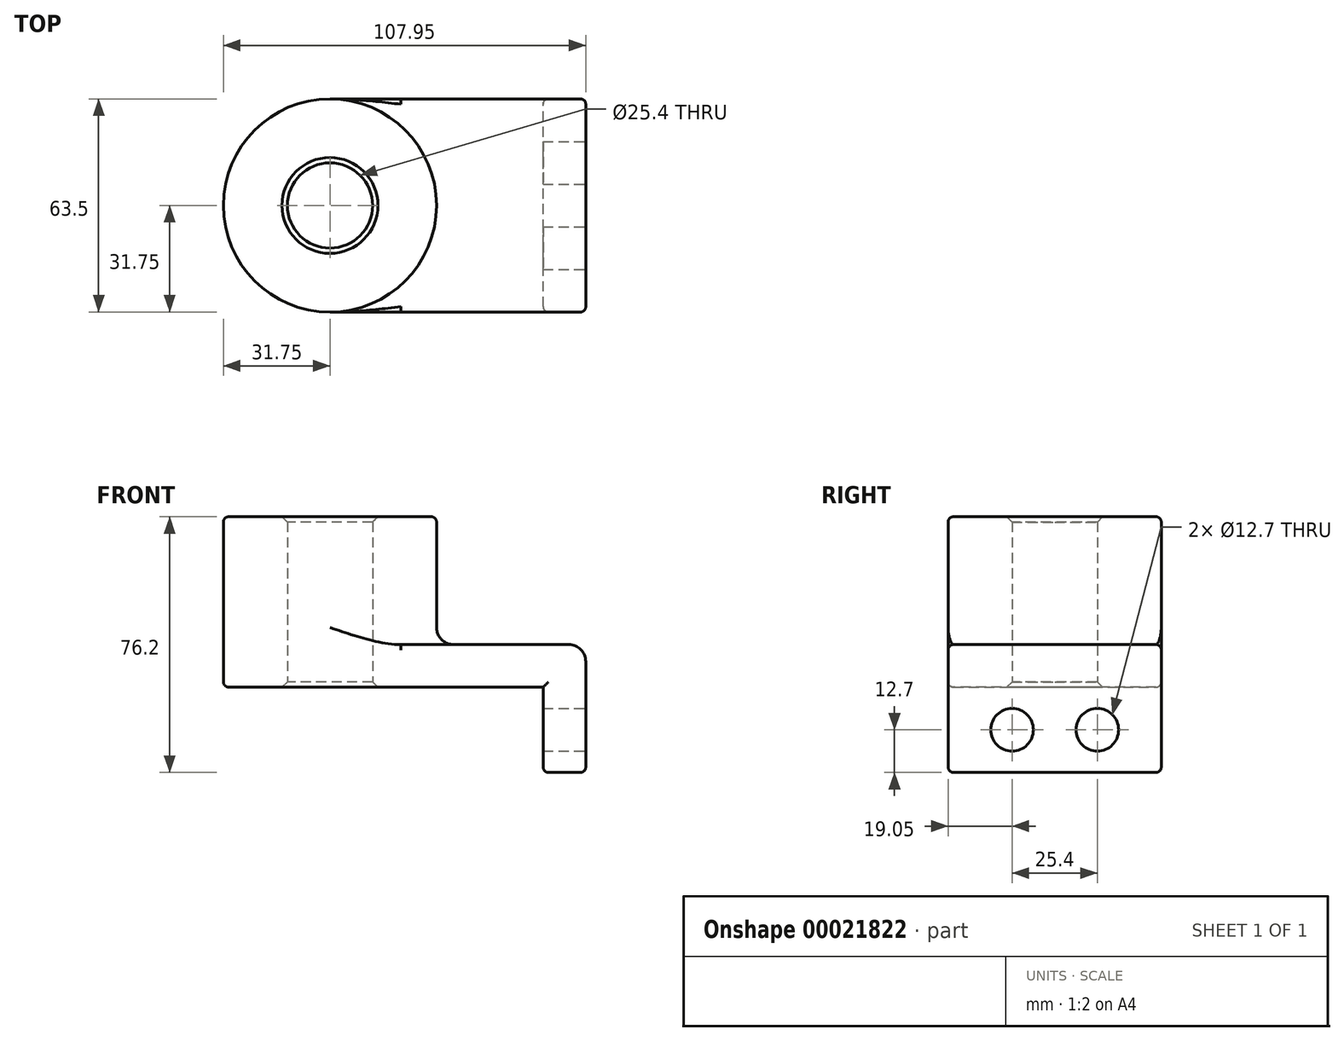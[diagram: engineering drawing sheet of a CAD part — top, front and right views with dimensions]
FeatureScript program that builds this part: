
annotation { "Feature Type Name" : "Feature", "Feature Type Description" : "" }
export const myFeature = defineFeature(function(context is Context, id is Id, definition is map)
    precondition{}
    {
        {
            var Q0;
            Q0=qCreatedBy(makeId("Top.planeOp"),FACE);
            var sketch = newSketch(context, id + "F0", { "sketchPlane" : qUnion([Q0])});
            skLineSegment(sketch, "E0.rect.bottom", {"start": v(38.1, 31.75) * mm, "end": v(-38.1, 31.75) * mm});
            skLineSegment(sketch, "E0.rect.top", {"start": v(38.1, -31.75) * mm, "end": v(-38.1, -31.75) * mm});
            skLineSegment(sketch, "E0.rect.left", {"start": v(38.1, 31.75) * mm, "end": v(38.1, -31.75) * mm});
            skLineSegment(sketch, "E0.rect.right", {"start": v(-38.1, 31.75) * mm, "end": v(-38.1, -31.75) * mm});
            skPoint(sketch, "E0.rect.middle", {"position": v(0, 0) * mm});
            skCircle(sketch, "E1", {"center": v(-38.1, 0) * mm, "radius": 31.75 * mm});
            skCircle(sketch, "E2", {"center": v(-38.1, 0) * mm, "radius": 12.7 * mm});
            skSolve(sketch);
        }
        {
            var Q0;
            Q0 = qSketchRegion(id + "F0", true);
            extrude(context, id + "F1", {"entities" : qUnion([Q0]), "depth" : 12.7 * mm});
        }
        {
            var Q0;
            {var subQ0=sQuery(id+"F0.wireOp",EDGE,"E2");var subQ1=sQuery(id+"F0.wireOp",EDGE,"E0.rect.right");var subQ3=makeQuery(id+"F0.imprint","INTERSECT",VERTEX,{"disambiguationData":[OD(0.0)],"derivedFrom":[subQ1,subQ0]});Q0=makeQuery(id+"F0.imprint","IMPRINT",FACE,{"disambiguationData":[TD([[makeQuery(id+"F0.imprint","IMPRINT",EDGE,{"disambiguationData":[TD([[subQ3,-1.0]])],"derivedFrom":subQ0}),-1.0]])]});}
            var Q1;
            {var subQ0=sQuery(id+"F0.wireOp",EDGE,"E2");var subQ1=sQuery(id+"F0.wireOp",EDGE,"E0.rect.right");var subQ3=makeQuery(id+"F0.imprint","INTERSECT",VERTEX,{"disambiguationData":[OD(0.0)],"derivedFrom":[subQ1,subQ0]});Q1=makeQuery(id+"F0.imprint","IMPRINT",FACE,{"disambiguationData":[TD([[makeQuery(id+"F0.imprint","IMPRINT",EDGE,{"disambiguationData":[TD([[subQ3,1.0]])],"derivedFrom":subQ0}),-1.0]])]});}
            extrude(context, id + "F2", {"entities" : qUnion([Q0, Q1]), "operationType" : NewBodyOperationType.ADD, "depth" : 50.8 * mm});
        }
        {
            var Q0;
            Q0=makeQuery(id+"F1.opExtrude","SWEPT_FACE",FACE,{"disambiguationData":[OSD([sQuery(id+"F0.wireOp",EDGE,"E0.rect.left")])]});
            var sketch = newSketch(context, id + "F3", { "sketchPlane" : qUnion([Q0])});
            skLineSegment(sketch, "E3.bottom", {"start": v(-31.75, 12.7) * mm, "end": v(31.75, 12.7) * mm});
            skLineSegment(sketch, "E3.top", {"start": v(-31.75, -25.4) * mm, "end": v(31.75, -25.4) * mm});
            skLineSegment(sketch, "E3.left", {"start": v(-31.75, 12.7) * mm, "end": v(-31.75, -25.4) * mm});
            skLineSegment(sketch, "E3.right", {"start": v(31.75, 12.7) * mm, "end": v(31.75, -25.4) * mm});
            skCircle(sketch, "E4", {"center": v(-12.7, -12.7) * mm, "radius": 6.35 * mm});
            skLineSegment(sketch, "E5", {"start": v(0, 0) * mm, "end": v(0, -25.4) * mm, "construction": true});
            skCircle(sketch, "E6.MirrorC", {"center": v(12.7, -12.7) * mm, "radius": 6.35 * mm});
            skSolve(sketch);
        }
        {
            var Q0;
            Q0 = qSketchRegion(id + "F3", true);
            extrude(context, id + "F4", {"entities" : qUnion([Q0]), "operationType" : NewBodyOperationType.ADD, "oppositeDirection" : true, "depth" : 12.7 * mm});
        }
        {
            var Q0;
            {var subQ0=sQuery(id+"F0.wireOp",EDGE,"E1");Q0=makeQuery(id+"F2.boolean.opBoolean","INTERSECT",EDGE,{"derivedFrom":[makeQuery(id+"F1.opExtrude","CAP_FACE",FACE,{"disambiguationData":[OSD([sQuery(id+"F0.wireOp",EDGE,"E0.rect.bottom"),sQuery(id+"F0.wireOp",EDGE,"E0.rect.top"),sQuery(id+"F0.wireOp",EDGE,"E0.rect.left"),subQ0,sQuery(id+"F0.wireOp",EDGE,"E2")])],"isStart":false}),makeQuery(id+"F2.opExtrude","SWEPT_FACE",FACE,{"disambiguationData":[OSD([subQ0])]})]});}
            var Q1;
            Q1=makeQuery(id+"F1.opExtrude","CAP_EDGE",EDGE,{"disambiguationData":[OSD([sQuery(id+"F0.wireOp",EDGE,"E0.rect.left")])],"isStart":false});
            fillet(context, id + "F5", {"entities" : qUnion([Q0, Q1]), "radius" : 5.08 * mm, "tangentPropagation" : true, "allowEdgeOverflow" : false});
        }
        {
            var Q0;
            Q0=makeQuery(id+"F4.boolean.opBoolean","MERGE",FACE,{"derivedFrom":[makeQuery(id+"F1.opExtrude","SWEPT_FACE",FACE,{"disambiguationData":[OSD([sQuery(id+"F0.wireOp",EDGE,"E0.rect.top")])]}),makeQuery(id+"F4.opExtrude","SWEPT_FACE",FACE,{"disambiguationData":[OSD([sQuery(id+"F3.wireOp",EDGE,"E3.left")])]})]});
            var Q1;
            Q1=makeQuery(id+"F4.boolean.opBoolean","MERGE",FACE,{"derivedFrom":[makeQuery(id+"F1.opExtrude","SWEPT_FACE",FACE,{"disambiguationData":[OSD([sQuery(id+"F0.wireOp",EDGE,"E0.rect.bottom")])]}),makeQuery(id+"F4.opExtrude","SWEPT_FACE",FACE,{"disambiguationData":[OSD([sQuery(id+"F3.wireOp",EDGE,"E3.right")])]})]});
            var Q2;
            Q2=makeQuery(id+"F4.opExtrude","SWEPT_FACE",FACE,{"disambiguationData":[OSD([sQuery(id+"F3.wireOp",EDGE,"E3.top")])]});
            var Q3;
            Q3=makeQuery(id+"F2.opExtrude","CAP_EDGE",EDGE,{"disambiguationData":[OSD([sQuery(id+"F0.wireOp",EDGE,"E1")])],"isStart":false});
            fillet(context, id + "F6", {"entities" : qUnion([Q0, Q1, Q2, Q3]), "radius" : 1.59 * mm, "tangentPropagation" : true, "allowEdgeOverflow" : false});
        }
        {
            var Q0;
            {var subQ0=sQuery(id+"F0.wireOp",EDGE,"E2");Q0=makeQuery(id+"F2.boolean.opBoolean","MERGE",FACE,{"derivedFrom":[makeQuery(id+"F1.opExtrude","SWEPT_FACE",FACE,{"disambiguationData":[OSD([subQ0])]}),makeQuery(id+"F2.opExtrude","SWEPT_FACE",FACE,{"disambiguationData":[OSD([subQ0])]})]});}
            chamfer(context, id + "F7", {"entities" : qUnion([Q0]), "width" : 1.59 * mm, "tangentPropagation" : true});
        }
    });
